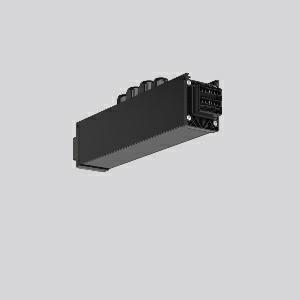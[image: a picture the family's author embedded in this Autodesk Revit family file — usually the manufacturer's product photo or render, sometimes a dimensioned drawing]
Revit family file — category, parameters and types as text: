
# Revit family: linedo_mitteleinspeisung_7pol_s_s_982698_003_5_f3b1
name_source: partatom
category: Lighting Fixtures
units: mm (PartAtom-declared; Revit-internal decimal feet)

## family parameters
Cut with Voids When Loaded = No
Host = Face
Light Source = No
Part Type = Normal
Room Calculation Point = No
Round Connector Dimension = Use Diameter
Shared = No

## types (1)
- LINEDO_Mitteleinspeisung_7pol_S_S
    Apparent Load = 0 VA
    Default Elevation = 1800 mm
    Description = Series: LINEDO
Middle power feed, 7-pole, connection plug / plug. Housing: extruded aluminium profile, powder-coated. Cover made of plastic, surface like housing. LINEDO plug system, plastic, black. 4 cable glands (2 x M20 and 2 x M25). Cable glands on top. Easy connection for rigid or flexible wires.
Colour: black
Length: 349 mm
Width: 58 mm
Height: 76 mm
Weight: 751 g
    Height = 76 mm
    Lamp = 0 x
    Length = 349 mm
    Luminous efficacy = 0 lm/W
    Manufacturer = RZB
    ModVariant = No
    Model = 982698.003.5
    Mounting Place = Ceiling
    Mounting Type = Surface mounted, Pendant
    Number of Poles = 1
    OnlyDefault = Yes
    Power Factor = 1
    Product Name = LINEDO_Mitteleinspeisung_7pol_S_S
    Product group = Surface mounted continuous line luminaire system
    ProductGroupID = 310
    Protection Class = Protection class I
    Protection Degree = IP 54
    RLX_Detail_Level = 1
    RLX_Emergency_Light_Flux = 0 lm
    RLX_Emergency_Type = 0
    RLX_Emergency_Type_DB = No
    RlxData = <blob elided: 23385 chars, md5=6e3ed227>
    Standby Power = 0 W
    System Light Flux = 0 lm
    System Power = 0 W
    Type Comments = Product without accessories
    Type Image = 982698.003.2.jpg
    URL = http://relux.com
    VarID = ---
    Voltage = 0 V
    Weight = 0.00 kg
    Width = 58 mm

## geometry (parser evidence)
native form markers: Blend x4, Sweep x10
no freeform markers — native parametric forms only
